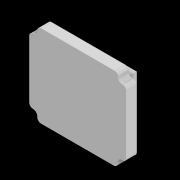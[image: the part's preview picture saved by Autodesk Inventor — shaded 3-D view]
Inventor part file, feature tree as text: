
AUTODESK INVENTOR PART (.ipt)
format: ipt  version: 2020 (Build 240168000, 168)  size: 151,552 bytes
history: native  units: in
note: dims shown in document units (in); Inventor stores cm internally (conversion verified against a paired STEP export)
features: extrude x3, imported_body x1, other x1
ambient origin geometry x8: Origin, YZ Plane, XZ Plane, XY Plane, X Axis, Y Axis, Z Axis, Center Point
bodies: Solid1 (feature_tree)
feature tree (5):
  imported_body  "Base"
  extrude  "BaseFeature"  Depth=0.15in TaperAngle=0.0deg
  extrude  "LogoFeature"  Depth=0.2in TaperAngle=0.0deg
  extrude  "LogoDetailFeature"  Depth=0.2in TaperAngle=0.0deg
  other  "LogoDetail"
